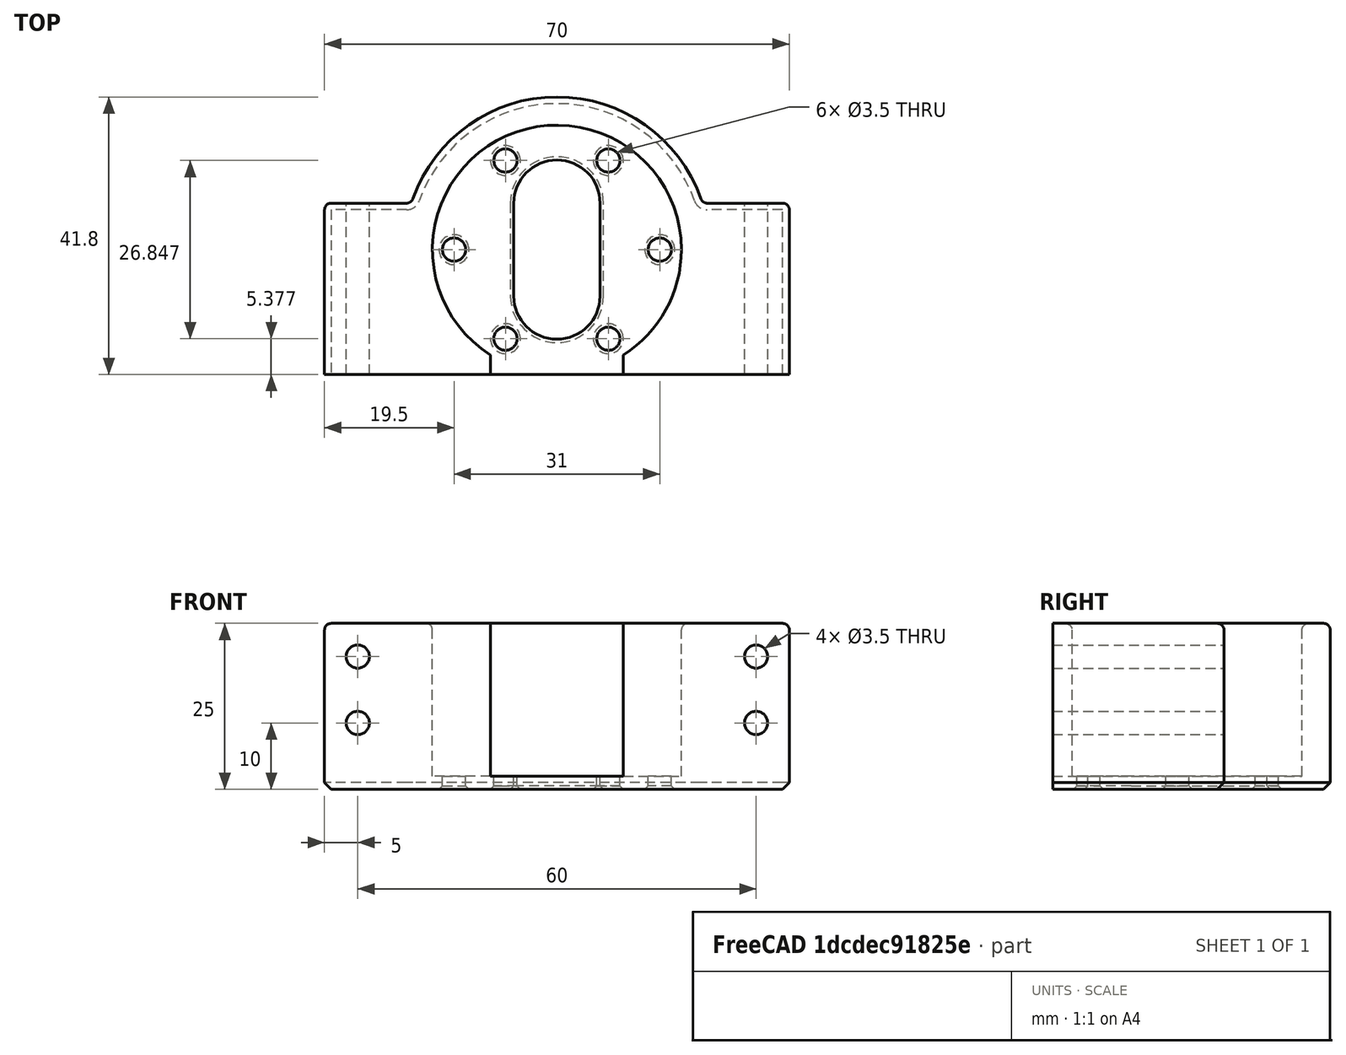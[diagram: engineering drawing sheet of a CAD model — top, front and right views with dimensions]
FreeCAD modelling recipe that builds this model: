
FCSTD DOCUMENT  (FreeCAD 0.17R13541 (Git))
Label: porta_motor
License: All rights reserved
LicenseURL: http://en.wikipedia.org/wiki/All_rights_reserved
objects: Part::Cylinder×6, Part::Box×4, Part::MultiFuse×4, Part::Cut×4, Part::FeaturePython×2, Part::Chamfer×2, Part::Fillet×1
note: 23 computed .brp shape members not serialized (recipe doc carries the construction recipe); baked Part::Feature solids carry a one-line shape summary decoded from their .brp

FEATURE [Part::Cylinder] Cylinder  label="Cilindro"
  Angle = 360
  AttacherType = Attacher::AttachEngine3D
  Height = 25
  Radius = 23
FEATURE [Part::Box] Box  label="Cubo"
  AttacherType = Attacher::AttachEngine3D
  Height = 25
  Length = 70
  Placement = pos=(-35,-23,0) rot=(0,0,1;0rad)
  Width = 30
FEATURE [Part::Cylinder] Cylinder001  label="Cilindro001"
  Angle = 360
  AttacherType = Attacher::AttachEngine3D
  Height = 25
  Placement = pos=(0,0,2) rot=(0,0,1;0rad)
  Radius = 18.75
FEATURE [Part::MultiFuse] Fusion
  Refine = true
  Shapes = -> [Box,Cylinder]
FEATURE [Part::Cut] Cut
  Base = -> Fusion
  Refine = true
  Tool = -> Cylinder001
FEATURE [Part::Cylinder] Cylinder002  label="Cilindro002"
  Angle = 360
  AttacherType = Attacher::AttachEngine3D
  Height = 60
  Placement = pos=(-30,-30,10) rot=(-1,0,0;1.5708rad)
  Radius = 1.75
FEATURE [Part::FeaturePython] Array  label="tornillos"  # Draft array (typed FeaturePython)
  Angle = 360
  ArrayType = 0
  Axis = (0,0,1)
  Base = -> Cylinder002
  Center = (0,0,0)
  Fuse = false
  IntervalAxis = (0,0,0)
  IntervalX = (60,0,0)
  IntervalY = (0,1,0)
  IntervalZ = (0,0,10)
  NumberPolar = 1
  NumberX = 2
  NumberY = 1
  NumberZ = 2
FEATURE [Part::Fillet] Fillet
  Base = -> Cut
  Edges = 12 edges r=1: [Edge1,Edge2,Edge3,Edge7,Edge8,Edge9,Edge10,Edge11,Edge12,Edge14,Edge18,Edge19]
FEATURE [Part::Chamfer] Chamfer
  Base = -> Fillet
  Edges = 12 edges r=1: [Edge1,Edge5,Edge6,Edge7,Edge8,Edge9,Edge10,Edge11,Edge12,Edge13,Edge14,Edge15]
FEATURE [Part::Cylinder] Cylinder003  label="Cilindro003"
  Angle = 360
  AttacherType = Attacher::AttachEngine3D
  Height = 10
  Placement = pos=(15.5,0,0) rot=(0,0,1;0rad)
  Radius = 1.75
FEATURE [Part::Cylinder] Cylinder004  label="Cilindro004"
  Angle = 360
  AttacherType = Attacher::AttachEngine3D
  Height = 10
  Placement = pos=(0,-7,0) rot=(0,0,1;0rad)
  Radius = 6.5
FEATURE [Part::Cylinder] Cylinder005  label="Cilindro005"
  Angle = 360
  AttacherType = Attacher::AttachEngine3D
  Height = 10
  Placement = pos=(0,7,0) rot=(0,0,1;0rad)
  Radius = 6.5
FEATURE [Part::Box] Box001  label="Cubo001"
  AttacherType = Attacher::AttachEngine3D
  Height = 10
  Length = 13
  Placement = pos=(-6.5,-7,0) rot=(0,0,1;0rad)
  Width = 14
FEATURE [Part::MultiFuse] Fusion001
  Refine = true
  Shapes = -> [Box001,Cylinder005,Cylinder004]
FEATURE [Part::FeaturePython] Array001  # Draft array (typed FeaturePython)
  Angle = 360
  ArrayType = 1
  Axis = (0,0,1)
  Base = -> Cylinder003
  Center = (0,0,0)
  Fuse = false
  IntervalAxis = (0,0,0)
  IntervalX = (1,0,0)
  IntervalY = (0,1,0)
  IntervalZ = (0,0,0)
  NumberPolar = 6
  NumberX = 2
  NumberY = 2
  NumberZ = 1
FEATURE [Part::MultiFuse] Fusion002
  Refine = true
  Shapes = -> [Fusion001,Array001]
FEATURE [Part::Cut] Cut001
  Base = -> Chamfer
  Refine = true
  Tool = -> Fusion002
FEATURE [Part::Cut] Cut002
  Base = -> Cut001
  Refine = true
  Tool = -> Array
FEATURE [Part::Chamfer] Chamfer001
  Base = -> Cut002
  Edges = 10 edges r=0.5: [Edge32,Edge33,Edge34,Edge35,Edge36,Edge37,Edge38,Edge39,Edge40,Edge41]
FEATURE [Part::Box] Box002  label="Cubo002"
  AttacherType = Attacher::AttachEngine3D
  Height = 25
  Length = 100
  Placement = pos=(-50,-23,0) rot=(0,0,1;0rad)
  Width = 4.2
FEATURE [Part::Box] Box003  label="Cubo003"
  AttacherType = Attacher::AttachEngine3D
  Height = 25
  Length = 20
  Placement = pos=(-10,-19,2) rot=(0,0,1;0rad)
  Width = 4.2
FEATURE [Part::MultiFuse] Fusion003
  Refine = true
  Shapes = -> [Box002,Box003]
FEATURE [Part::Cut] Cut003  label="portamotor"
  Base = -> Chamfer001
  Refine = true
  Tool = -> Fusion003
